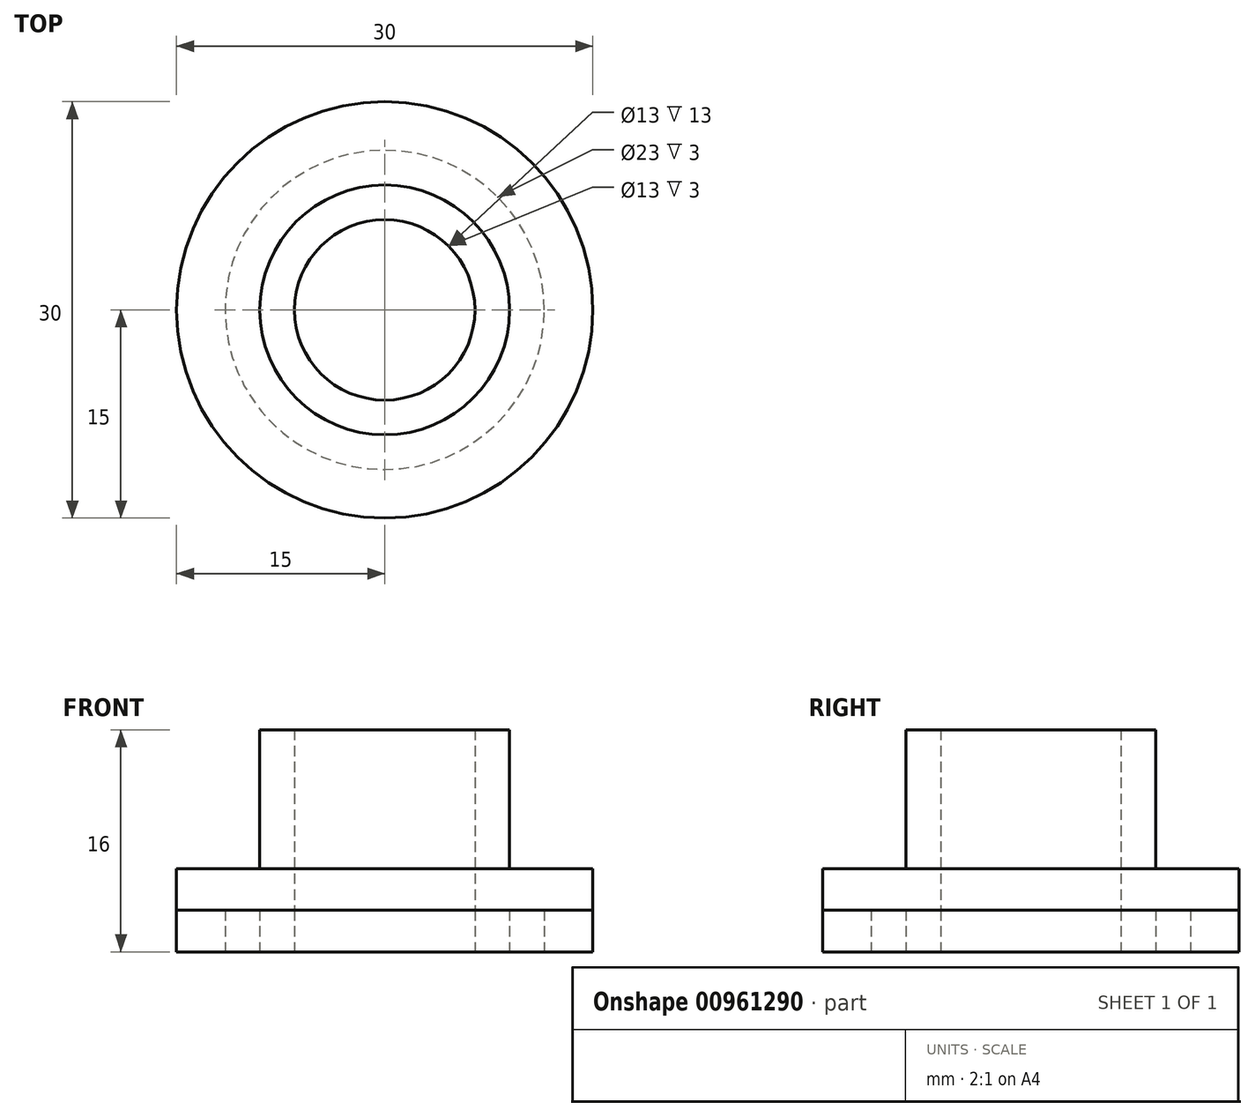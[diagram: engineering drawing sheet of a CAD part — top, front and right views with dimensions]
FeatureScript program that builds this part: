
annotation { "Feature Type Name" : "Feature", "Feature Type Description" : "" }
export const myFeature = defineFeature(function(context is Context, id is Id, definition is map)
    precondition{}
    {
        {
            var Q0;
            Q0=qCreatedBy(makeId("Top.planeOp"),FACE);
            var sketch = newSketch(context, id + "F0", { "sketchPlane" : qUnion([Q0])});
            skCircle(sketch, "E0", {"center": v(0, 0) * mm, "radius": 15 * mm});
            skCircle(sketch, "E1", {"center": v(0, 0) * mm, "radius": 6.5 * mm});
            skCircle(sketch, "E2", {"center": v(0, 0) * mm, "radius": 9 * mm});
            skCircle(sketch, "E3", {"center": v(0, 0) * mm, "radius": 11.5 * mm});
            skSolve(sketch);
        }
        {
            var Q0;
            Q0=makeQuery(id+"F0.imprint","IMPRINT",FACE,{"disambiguationData":[TD([[makeQuery(id+"F0.imprint","IMPRINT",EDGE,{"derivedFrom":sQuery(id+"F0.wireOp",EDGE,"E0")}),1.0]])]});
            var Q1;
            Q1=makeQuery(id+"F0.imprint","IMPRINT",FACE,{"disambiguationData":[TD([[makeQuery(id+"F0.imprint","IMPRINT",EDGE,{"derivedFrom":sQuery(id+"F0.wireOp",EDGE,"E1")}),-1.0]])]});
            var Q2;
            Q2 = qSketchRegion(id + "Fdrr8pzUyZRIJFD_1", true);
            extrude(context, id + "F1", {"entities" : qUnion([Q0, Q1, Q2]), "depth" : 3 * mm, "offsetDistance" : 25 * mm});
        }
        {
            var Q0;
            Q0=makeQuery(id+"F1.opExtrude","CAP_FACE",FACE,{"disambiguationData":[OSD([sQuery(id+"F0.wireOp",EDGE,"E0"),sQuery(id+"F0.wireOp",EDGE,"E3")])],"isStart":false});
            var sketch = newSketch(context, id + "F2", { "sketchPlane" : qUnion([Q0])});
            skCircle(sketch, "E4", {"center": v(0, 0) * mm, "radius": 6.5 * mm});
            skSolve(sketch);
        }
        {
            var Q0;
            Q0=makeQuery(id+"F2.imprint","IMPRINT",FACE,{"disambiguationData":[TD([[makeQuery(id+"F2.imprint","IMPRINT",EDGE,{"derivedFrom":makeQuery(id+"F1.opExtrude","CAP_EDGE",EDGE,{"disambiguationData":[OSD([sQuery(id+"F0.wireOp",EDGE,"E0")])],"isStart":false})}),1.0]])]});
            var Q1;
            Q1=makeQuery(id+"F2.imprint","IMPRINT",FACE,{"disambiguationData":[TD([[makeQuery(id+"F2.imprint","IMPRINT",EDGE,{"derivedFrom":sQuery(id+"F2.wireOp",EDGE,"E4")}),-1.0]])]});
            extrude(context, id + "F3", {"entities" : qUnion([Q0, Q1]), "depth" : 3 * mm, "offsetDistance" : 25 * mm});
        }
        {
            var Q0;
            Q0=makeQuery(id+"F3.opExtrude","CAP_FACE",FACE,{"disambiguationData":[OSD([sQuery(id+"F0.wireOp",EDGE,"E0"),sQuery(id+"F2.wireOp",EDGE,"E4")])],"isStart":false});
            var sketch = newSketch(context, id + "F4", { "sketchPlane" : qUnion([Q0])});
            skCircle(sketch, "E5", {"center": v(0, 0) * mm, "radius": 9 * mm});
            skSolve(sketch);
        }
        {
            var Q0;
            Q0=makeQuery(id+"F4.imprint","IMPRINT",FACE,{"disambiguationData":[TD([[makeQuery(id+"F4.imprint","IMPRINT",EDGE,{"derivedFrom":sQuery(id+"F4.wireOp",EDGE,"E5")}),1.0]])]});
            extrude(context, id + "F5", {"entities" : qUnion([Q0]), "operationType" : NewBodyOperationType.ADD, "depth" : 10 * mm, "offsetDistance" : 25 * mm});
        }
    });
